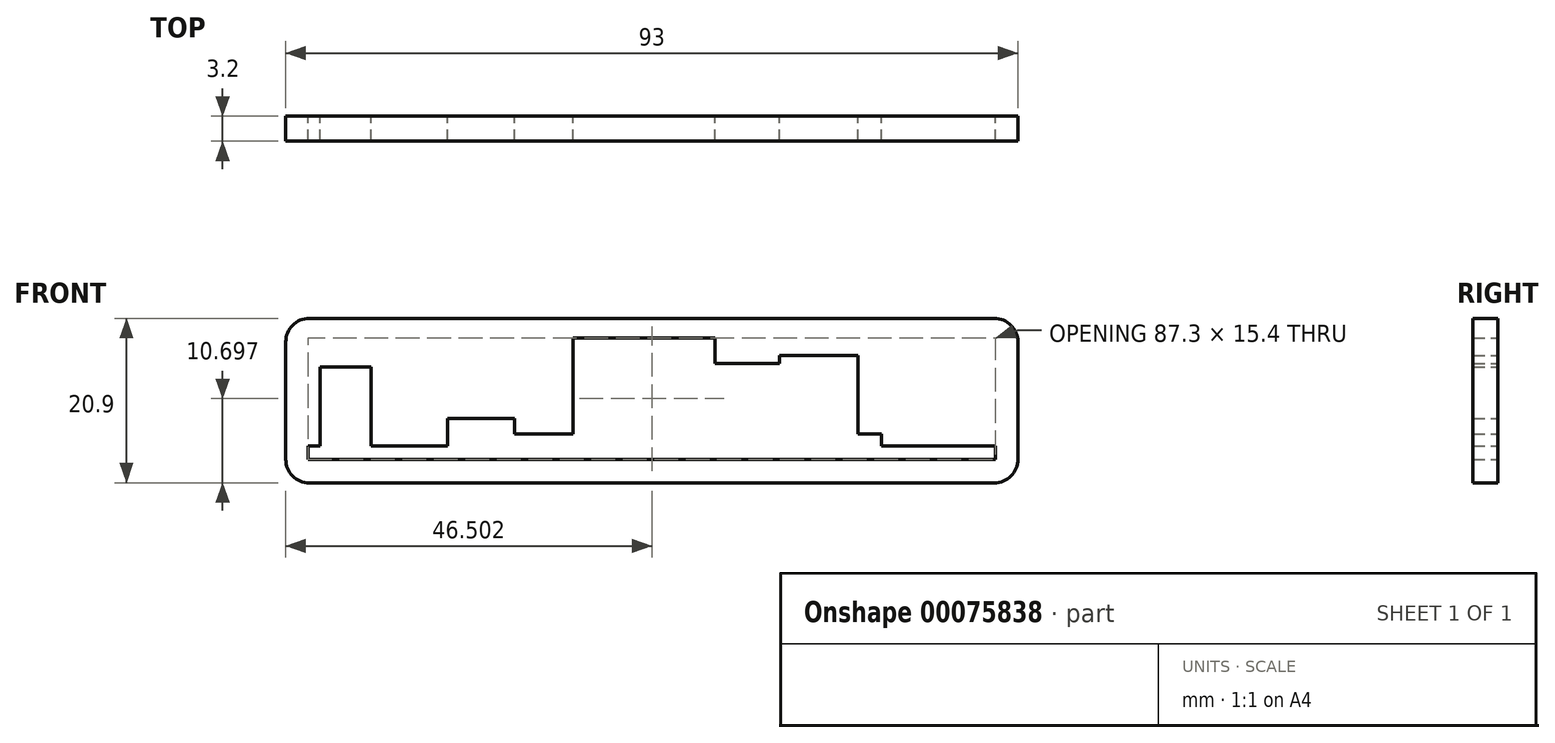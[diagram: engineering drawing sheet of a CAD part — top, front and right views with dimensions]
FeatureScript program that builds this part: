
annotation { "Feature Type Name" : "Feature", "Feature Type Description" : "" }
export const myFeature = defineFeature(function(context is Context, id is Id, definition is map)
    precondition{}
    {
        {
            var Q0;
            Q0=qCreatedBy(makeId("Front.planeOp"),FACE);
            var sketch = newSketch(context, id + "F0", { "sketchPlane" : qUnion([Q0])});
            skLineSegment(sketch, "E0", {"start": v(13.24, -8.68) * mm, "end": v(13.24, 1.32) * mm});
            skLineSegment(sketch, "E1", {"start": v(13.24, 1.32) * mm, "end": v(3.24, 1.32) * mm});
            skLineSegment(sketch, "E2", {"start": v(3.24, 1.32) * mm, "end": v(3.24, 0.32) * mm});
            skLineSegment(sketch, "E3", {"start": v(3.24, 0.32) * mm, "end": v(-4.96, 0.32) * mm});
            skLineSegment(sketch, "E4", {"start": v(-4.96, 0.32) * mm, "end": v(-4.96, 3.52) * mm});
            skLineSegment(sketch, "E5", {"start": v(-4.96, 3.52) * mm, "end": v(-22.96, 3.52) * mm});
            skLineSegment(sketch, "E6", {"start": v(-22.96, 3.52) * mm, "end": v(-22.96, -8.68) * mm});
            skLineSegment(sketch, "E7", {"start": v(-22.96, -8.68) * mm, "end": v(-30.4, -8.68) * mm});
            skLineSegment(sketch, "E8", {"start": v(-30.4, -8.68) * mm, "end": v(-30.4, -6.68) * mm});
            skLineSegment(sketch, "E9", {"start": v(-30.4, -6.68) * mm, "end": v(-38.9, -6.68) * mm});
            skLineSegment(sketch, "E10", {"start": v(-38.9, -6.68) * mm, "end": v(-38.9, -10.18) * mm});
            skLineSegment(sketch, "E11", {"start": v(-56.6, -10.18) * mm, "end": v(-56.6, -11.88) * mm});
            skLineSegment(sketch, "E12", {"start": v(-56.6, -11.88) * mm, "end": v(30.7, -11.88) * mm});
            skLineSegment(sketch, "E13", {"start": v(30.7, -11.88) * mm, "end": v(30.7, -10.18) * mm});
            skLineSegment(sketch, "E14", {"start": v(-56.6, -10.18) * mm, "end": v(-55.1, -10.18) * mm});
            skLineSegment(sketch, "E15", {"start": v(-55.1, -10.18) * mm, "end": v(-55.1, -0.18) * mm});
            skLineSegment(sketch, "E16", {"start": v(-55.1, -0.18) * mm, "end": v(-48.6, -0.18) * mm});
            skLineSegment(sketch, "E17", {"start": v(-48.6, -0.18) * mm, "end": v(-48.6, -10.18) * mm});
            skLineSegment(sketch, "E18", {"start": v(-48.6, -10.18) * mm, "end": v(-38.9, -10.18) * mm});
            skLineSegment(sketch, "E19", {"start": v(13.24, -8.68) * mm, "end": v(16.24, -8.68) * mm});
            skLineSegment(sketch, "E20", {"start": v(16.24, -8.68) * mm, "end": v(16.24, -10.18) * mm});
            skLineSegment(sketch, "E21", {"start": v(16.24, -10.18) * mm, "end": v(30.7, -10.18) * mm});
            skLineSegment(sketch, "E22.bottom", {"start": v(-56.46, 6.02) * mm, "end": v(30.54, 6.02) * mm});
            skLineSegment(sketch, "E22.top", {"start": v(-56.46, -14.88) * mm, "end": v(30.54, -14.88) * mm});
            skLineSegment(sketch, "E22.left", {"start": v(-59.46, 3.02) * mm, "end": v(-59.46, -11.88) * mm});
            skLineSegment(sketch, "E22.right", {"start": v(33.54, 3.02) * mm, "end": v(33.54, -11.88) * mm});
            skPoint(sketch, "E23.visualSharp", {"position": v(-59.46, 6.02) * mm});
            skArc(sketch, "E23.filletArc", {"start": v(-56.46, 6.02) * mm, "mid": v(-58.58, 5.14) * mm, "end": v(-59.46, 3.02) * mm});
            skPoint(sketch, "E24.visualSharp", {"position": v(33.54, 6.02) * mm});
            skArc(sketch, "E24.filletArc", {"start": v(33.54, 3.02) * mm, "mid": v(32.66, 5.14) * mm, "end": v(30.54, 6.02) * mm});
            skPoint(sketch, "E25.visualSharp", {"position": v(33.54, -14.88) * mm});
            skArc(sketch, "E25.filletArc", {"start": v(30.54, -14.88) * mm, "mid": v(32.66, -14) * mm, "end": v(33.54, -11.88) * mm});
            skPoint(sketch, "E26.visualSharp", {"position": v(-59.46, -14.88) * mm});
            skArc(sketch, "E26.filletArc", {"start": v(-59.46, -11.88) * mm, "mid": v(-58.58, -14) * mm, "end": v(-56.46, -14.88) * mm});
            skSolve(sketch);
        }
        {
            var Q0;
            Q0=makeQuery(id+"F0.imprint","IMPRINT",FACE,{"disambiguationData":[TD([[makeQuery(id+"F0.imprint","IMPRINT",EDGE,{"derivedFrom":sQuery(id+"F0.wireOp",EDGE,"E0")}),-1.0]])]});
            extrude(context, id + "F1", {"entities" : qUnion([Q0]), "depth" : 3.2 * mm});
        }
    });
